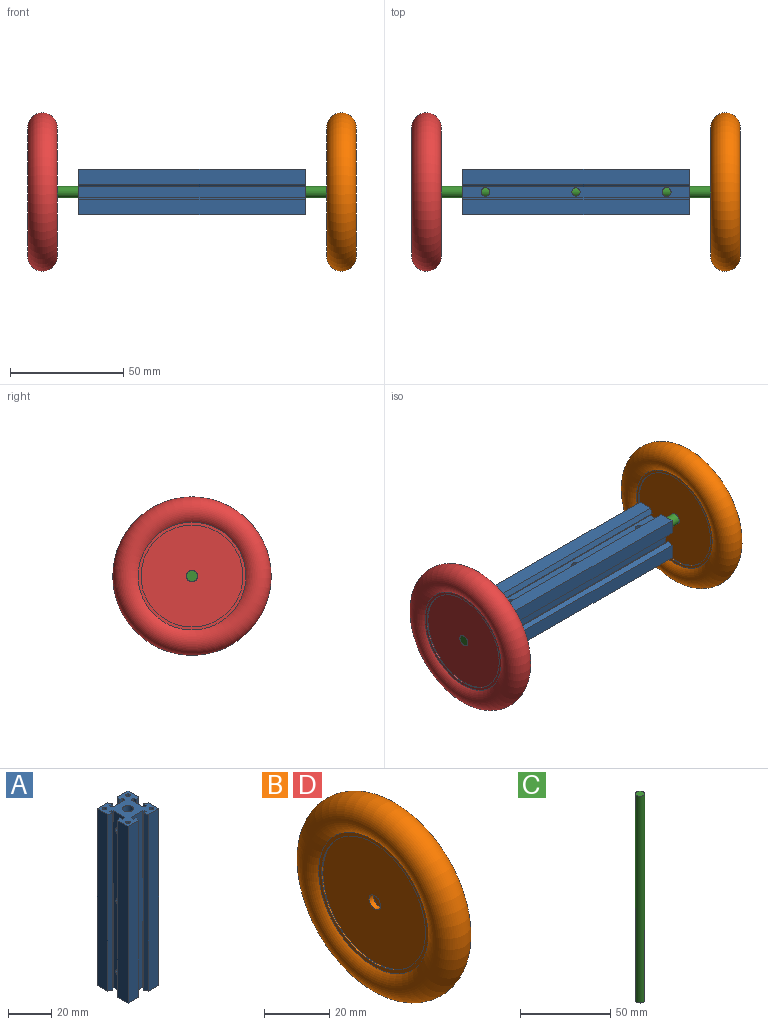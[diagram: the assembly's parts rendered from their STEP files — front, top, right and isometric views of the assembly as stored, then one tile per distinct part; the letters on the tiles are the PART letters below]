
ASSEMBLY  parts=4 mates=3
PART A: 57 faces, bbox 20x20x100 mm
  f0: plane 100x1.74mm, normal (-1,0,0), area 174.2mm2, adj f1,f47,f49,f50
  f1: plane 100x1.33mm, normal (0,1,0), area 133.2mm2, adj f0,f2,f49,f50
  f2: plane 100x0.44mm, normal (0.81,0.59,0), area 54mm2, adj f1,f3,f49,f50
  f3: plane 100x7.42mm, normal (1,0,0), area 707mm2, adj f2,f4,f49,f50,f51,f53,f55
  f4: plane 100x0.44mm, normal (0.81,-0.59,0), area 54mm2, adj f3,f5,f49,f50
  f5: plane 100x1.33mm, normal (0,-1,0), area 133.2mm2, adj f4,f6,f49,f50
  f6: plane 100x1.74mm, normal (-1,0,0), area 174.2mm2, adj f5,f7,f49,f50
  f7: plane 100x2.31mm, normal (0.39,-0.92,0), area 250.4mm2, adj f6,f8,f49,f50
  f8: plane 100x6.63mm, normal (1,0,0), area 663.1mm2, adj f7,f9,f49,f50
  f9: plane 100x6.63mm, normal (0,1,0), area 663.1mm2, adj f8,f10,f49,f50
  f10: plane 100x2.31mm, normal (-0.92,0.39,0), area 250.4mm2, adj f9,f11,f49,f50
  f11: plane 100x1.81mm, normal (0,-1,0), area 181.1mm2, adj f10,f12,f49,f50
  f12: plane 100x1.43mm, normal (-1,0,0), area 142.7mm2, adj f11,f13,f49,f50
  f13: plane 100x0.44mm, normal (-0.59,0.81,0), area 54mm2, adj f12,f14,f49,f50
  f14: plane 100x7.55mm, normal (0,1,0), area 755.2mm2, adj f13,f15,f49,f50
  f15: plane 100x0.44mm, normal (0.59,0.81,0), area 54mm2, adj f14,f16,f49,f50
  f16: plane 100x1.43mm, normal (1,0,0), area 142.7mm2, adj f15,f17,f49,f50
  f17: plane 100x1.81mm, normal (0,-1,0), area 181.1mm2, adj f16,f18,f49,f50
  f18: plane 100x2.31mm, normal (0.92,0.39,0), area 250.4mm2, adj f17,f19,f49,f50
  f19: plane 100x6.63mm, normal (0,1,0), area 663.1mm2, adj f18,f20,f49,f50
  f20: plane 100x6.63mm, normal (-1,0,0), area 663.1mm2, adj f19,f21,f49,f50
  f21: plane 100x2.31mm, normal (-0.39,-0.92,0), area 250.4mm2, adj f20,f22,f49,f50
  f22: plane 100x1.74mm, normal (1,0,0), area 174.2mm2, adj f21,f23,f49,f50
  f23: plane 100x1.33mm, normal (0,-1,0), area 133.2mm2, adj f22,f24,f49,f50
  f24: plane 100x0.44mm, normal (-0.81,-0.59,0), area 54mm2, adj f23,f25,f49,f50
  f25: plane 100x7.42mm, normal (-1,0,0), area 707mm2, adj f24,f26,f49,f50,f52,f54,f56
  f26: plane 100x0.44mm, normal (-0.81,0.59,0), area 54mm2, adj f25,f27,f49,f50
  f27: plane 100x1.33mm, normal (0,1,0), area 133.2mm2, adj f26,f28,f49,f50
  f28: plane 100x1.74mm, normal (1,0,0), area 174.2mm2, adj f27,f29,f49,f50
  f29: plane 100x2.31mm, normal (-0.39,0.92,0), area 250.4mm2, adj f28,f30,f49,f50
  f30: plane 100x6.63mm, normal (-1,0,0), area 663.1mm2, adj f29,f31,f49,f50
  f31: plane 100x6.63mm, normal (0,-1,0), area 663.1mm2, adj f30,f32,f49,f50
  f32: plane 100x2.31mm, normal (0.92,-0.39,0), area 250.4mm2, adj f31,f33,f49,f50
  f33: plane 100x1.81mm, normal (0,1,0), area 181.1mm2, adj f32,f34,f49,f50
  f34: plane 100x1.43mm, normal (1,0,0), area 142.7mm2, adj f33,f35,f49,f50
  f35: plane 100x0.44mm, normal (0.59,-0.81,0), area 54mm2, adj f34,f36,f49,f50
  f36: plane 100x7.55mm, normal (0,-1,0), area 755.2mm2, adj f35,f37,f49,f50
  f37: plane 100x0.44mm, normal (-0.59,-0.81,0), area 54mm2, adj f36,f38,f49,f50
  f38: plane 100x1.43mm, normal (-1,0,0), area 142.7mm2, adj f37,f39,f49,f50
  f39: plane 100x1.81mm, normal (0,1,0), area 181.1mm2, adj f38,f40,f49,f50
  f40: plane 100x2.31mm, normal (-0.92,-0.39,0), area 250.4mm2, adj f39,f41,f49,f50
  f41: plane 100x6.63mm, normal (0,-1,0), area 663.1mm2, adj f40,f42,f49,f50
  f42: plane 100x6.63mm, normal (1,0,0), area 663.1mm2, adj f41,f47,f49,f50
  f43: cylinder r=1mm len=100mm, axis (0,0,-1), area 628.3mm2, adj f49,f50
  f44: cylinder r=1mm len=100mm, axis (0,0,-1), area 628.3mm2, adj f49,f50
  f45: cylinder r=1mm len=100mm, axis (0,0,-1), area 628.3mm2, adj f49,f50
  f46: cylinder r=1mm len=100mm, axis (0,0,-1), area 628.3mm2, adj f49,f50
  f47: plane 100x2.31mm, normal (0.39,0.92,0), area 250.4mm2, adj f0,f42,f49,f50
  f48: cylinder r=2.5mm len=100mm, axis (0,0,-1), area 1494.9mm2, adj f49,f50,f51,f52,f53,f54,f55,f56
  f49: plane 20x20mm, normal (0,0,1), area 258.3mm2, adj f0,f1,f2,f3,f4,f5,f6,f7
  f50: plane 20x20mm, normal (0,0,-1), area 258.3mm2, adj f0,f1,f2,f3,f4,f5,f6,f7
  f51: cylinder r=1.92mm len=4.44mm, axis (1,0,0), area 47.9mm2, adj f3,f48
  f52: cylinder r=1.92mm len=4.44mm, axis (1,0,0), area 47.9mm2, adj f25,f48
  f53: cylinder r=1.82mm len=4.32mm, axis (1,0,0), area 44.7mm2, adj f3,f48
  f54: cylinder r=1.82mm len=4.32mm, axis (1,0,0), area 44.7mm2, adj f25,f48
  f55: cylinder r=2mm len=4.54mm, axis (1,0,0), area 50.4mm2, adj f3,f48
  f56: cylinder r=2mm len=4.54mm, axis (1,0,0), area 50.4mm2, adj f25,f48
PART B: 11 faces, bbox 9x75.8x75.8 mm
  f0: plane 47.6x47.6mm, normal (-1,0,0), area 189mm2, adj f1,f10
  f1: cylinder r=22.5mm len=45mm, axis (-1,0,0), area 70.7mm2, adj f0,f2
  f2: plane 45x45mm, normal (-1,0,0), area 1570.8mm2, adj f1,f3
  f3: cylinder r=2.5mm len=5mm, axis (-1,0,0), area 31.4mm2, adj f2,f4
  f4: plane 5x5mm, normal (-1,0,0), area 19.6mm2, adj f3
  f5: plane 5x5mm, normal (1,0,0), area 19.6mm2, adj f6
  f6: cylinder r=2.5mm len=5mm, axis (-1,0,0), area 31.4mm2, adj f5,f7
  f7: plane 45x45mm, normal (1,0,0), area 1570.8mm2, adj f6,f8
  f8: cylinder r=22.5mm len=45mm, axis (-1,0,0), area 70.7mm2, adj f7,f9
  f9: cone r=22.5mm half-angle=89.5deg, axis (1,0,0), area 189mm2, adj f8,f10
  f10: torus R=28.49mm, axis (-1,0,0), area 5904.5mm2, adj f0,f9
PART C: 3 faces, bbox 5x5x140 mm
  f0: cylinder r=2.5mm len=140mm, axis (0,0,-1), area 2199.1mm2, adj f1,f2
  f1: plane 5x5mm, normal (0,0,1), area 19.6mm2, adj f0
  f2: plane 5x5mm, normal (0,0,-1), area 19.6mm2, adj f0
PART D: same geometry as B
PLACE A rot(axis=(0,1,0),90deg) t=(287.49,203.77,44.95)mm
PLACE B t=(474.47,211.85,14.6)mm
PLACE C rot(axis=(0,1,0),90deg) t=(267.49,172.21,50.84)mm
PLACE D t=(342.47,211.85,14.6)mm
MATE slider C.f0 <-> A.f48  axis (-1,0,0) through (267.49,188.05,14.6)mm
MATE fastened B.f1 <-> C.f0  axis (1,0,0) through (407.49,188.05,14.6)mm
MATE fastened D.f1 <-> C.f0  axis (-1,0,0) through (267.49,188.05,14.6)mm
